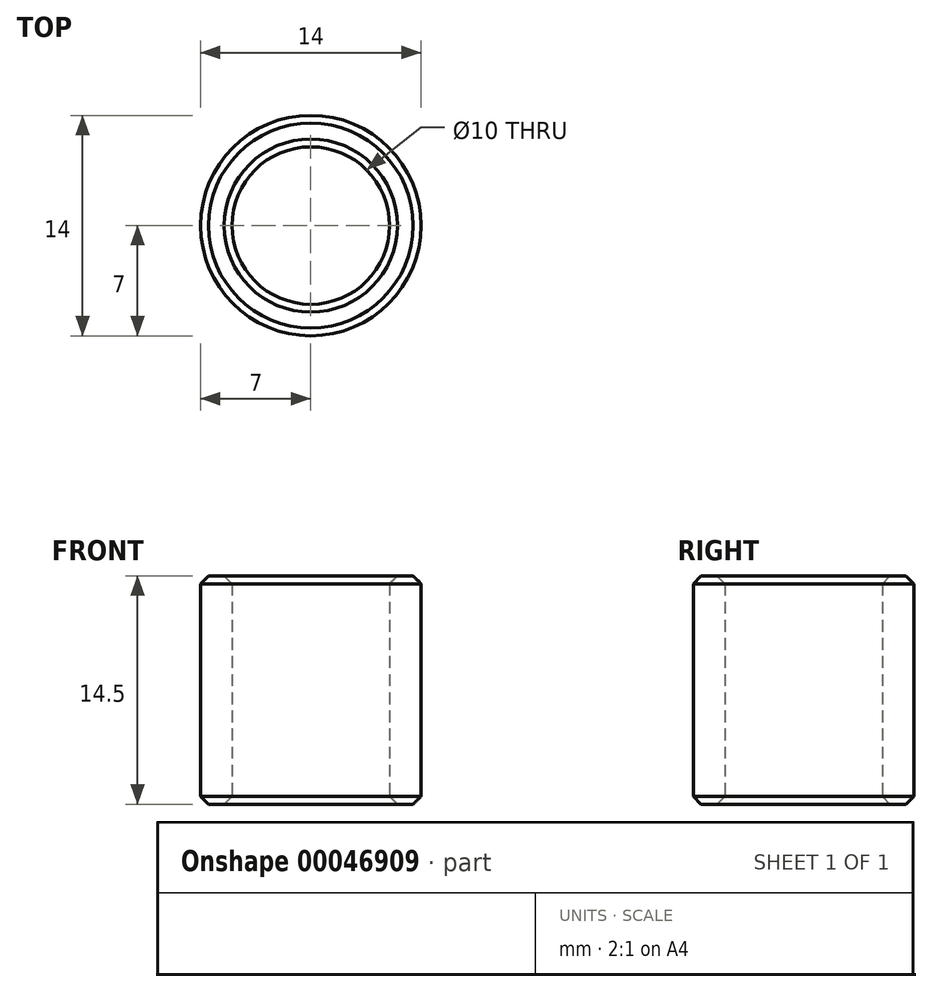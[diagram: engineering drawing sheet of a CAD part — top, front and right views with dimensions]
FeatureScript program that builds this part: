
annotation { "Feature Type Name" : "Feature", "Feature Type Description" : "" }
export const myFeature = defineFeature(function(context is Context, id is Id, definition is map)
    precondition{}
    {
        {
            var Q0;
            Q0=qCreatedBy(makeId("Top.planeOp"),FACE);
            var sketch = newSketch(context, id + "F0", { "sketchPlane" : qUnion([Q0])});
            skCircle(sketch, "E0", {"center": v(0, 0) * mm, "radius": 7 * mm});
            skCircle(sketch, "E1", {"center": v(0, 0) * mm, "radius": 5 * mm});
            skSolve(sketch);
        }
        {
            var Q0;
            Q0 = qSketchRegion(id + "F0", true);
            extrude(context, id + "F1", {"entities" : qUnion([Q0]), "depth" : 14.5 * mm});
        }
        {
            var Q0;
            Q0=makeQuery(id+"F1.opExtrude","CAP_FACE",FACE,{"disambiguationData":[OSD([sQuery(id+"F0.wireOp",EDGE,"E0"),sQuery(id+"F0.wireOp",EDGE,"E1")])],"isStart":false});
            var Q1;
            Q1=makeQuery(id+"F1.opExtrude","CAP_FACE",FACE,{"disambiguationData":[OSD([sQuery(id+"F0.wireOp",EDGE,"E0"),sQuery(id+"F0.wireOp",EDGE,"E1")])],"isStart":true});
            chamfer(context, id + "F2", {"entities" : qUnion([Q0, Q1]), "width" : .5 * mm, "tangentPropagation" : true});
        }
    });
